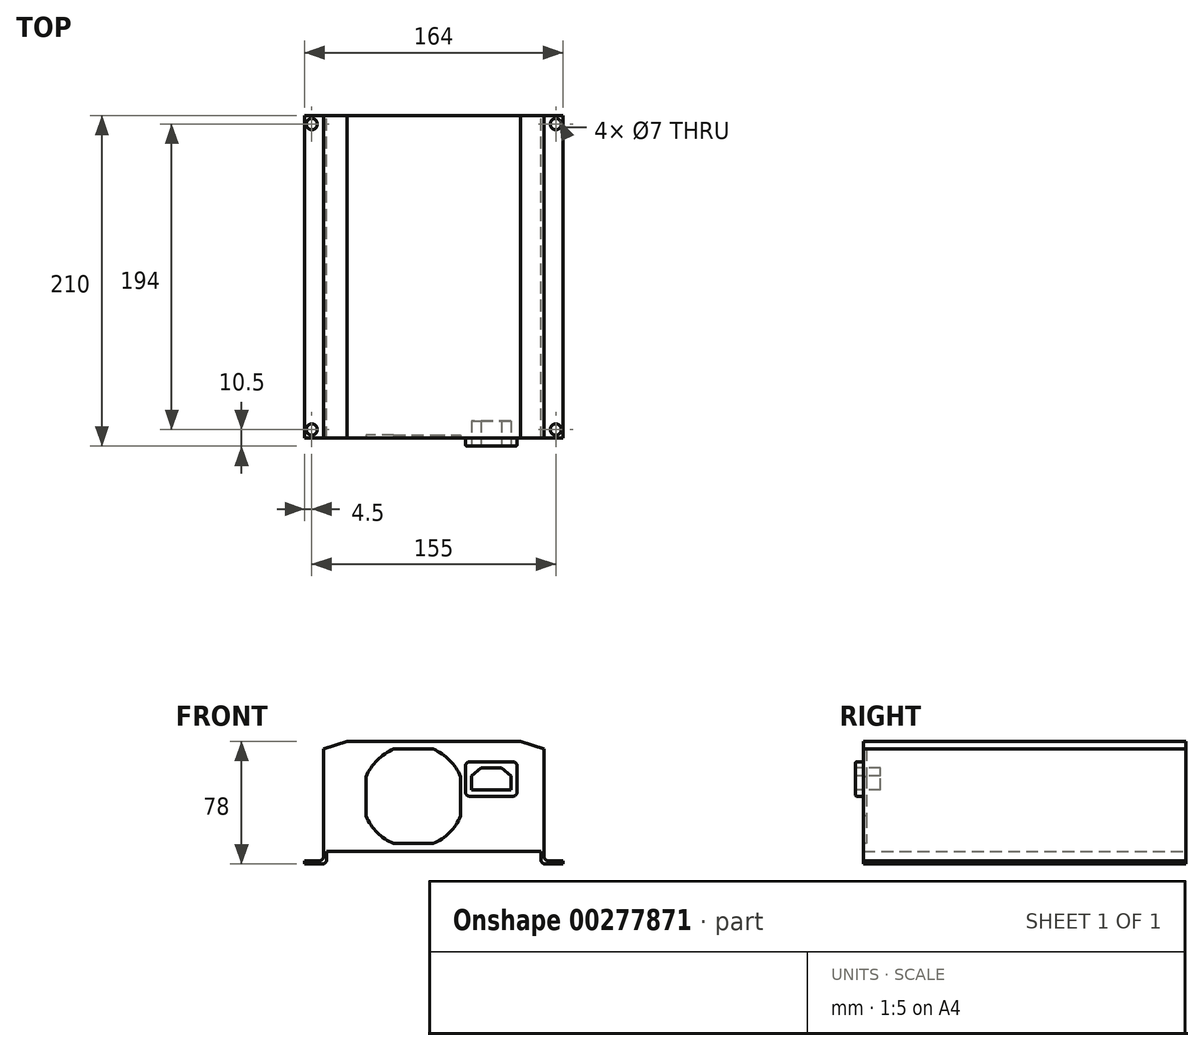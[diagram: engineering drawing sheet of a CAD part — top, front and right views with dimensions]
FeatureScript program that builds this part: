
annotation { "Feature Type Name" : "Feature", "Feature Type Description" : "" }
export const myFeature = defineFeature(function(context is Context, id is Id, definition is map)
    precondition{}
    {
        {
            var Q0;
            Q0=qCreatedBy(makeId("Front.planeOp"),FACE);
            var sketch = newSketch(context, id + "F0", { "sketchPlane" : qUnion([Q0])});
            skLineSegment(sketch, "E0", {"start": v(0, 70) * mm, "end": v(55, 70) * mm});
            skLineSegment(sketch, "E1", {"start": v(55, 70) * mm, "end": v(70, 65) * mm});
            skLineSegment(sketch, "E2", {"start": v(70, 65) * mm, "end": v(70, 0) * mm});
            skLineSegment(sketch, "E3", {"start": v(70, 0) * mm, "end": v(0, 0) * mm});
            skLineSegment(sketch, "E4.MirrorCS", {"start": v(0, 70) * mm, "end": v(-55, 70) * mm});
            skLineSegment(sketch, "E5.MirrorCS", {"start": v(-55, 70) * mm, "end": v(-70, 65) * mm});
            skLineSegment(sketch, "E6.MirrorCS", {"start": v(-70, 65) * mm, "end": v(-70, 0) * mm});
            skLineSegment(sketch, "E7.MirrorCS", {"start": v(-70, 0) * mm, "end": v(0, 0) * mm});
            skLineSegment(sketch, "E8", {"start": v(-70, 0) * mm, "end": v(-70, -3) * mm});
            skLineSegment(sketch, "E9", {"start": v(-73, -6) * mm, "end": v(-82, -6) * mm});
            skLineSegment(sketch, "E10", {"start": v(-82, -6) * mm, "end": v(-82, -8) * mm});
            skLineSegment(sketch, "E11", {"start": v(-82, -8) * mm, "end": v(-71, -8) * mm});
            skLineSegment(sketch, "E12", {"start": v(-68, -5) * mm, "end": v(-68, 0) * mm});
            skPoint(sketch, "E13.visualSharp", {"position": v(-70, -6) * mm});
            skArc(sketch, "E13.filletArc", {"start": v(-73, -6) * mm, "mid": v(-70.88, -5.12) * mm, "end": v(-70, -3) * mm});
            skPoint(sketch, "E14.visualSharp", {"position": v(-68, -8) * mm});
            skArc(sketch, "E14.filletArc", {"start": v(-71, -8) * mm, "mid": v(-68.88, -7.12) * mm, "end": v(-68, -5) * mm});
            skLineSegment(sketch, "E15.MirrorCS", {"start": v(82, -8) * mm, "end": v(71, -8) * mm});
            skLineSegment(sketch, "E16.MirrorCS", {"start": v(82, -6) * mm, "end": v(82, -8) * mm});
            skLineSegment(sketch, "E17.MirrorCS", {"start": v(73, -6) * mm, "end": v(82, -6) * mm});
            skArc(sketch, "E18.MirrorCS", {"start": v(73, -6) * mm, "mid": v(70.88, -5.12) * mm, "end": v(70, -3) * mm});
            skArc(sketch, "E19.MirrorCS", {"start": v(71, -8) * mm, "mid": v(68.88, -7.12) * mm, "end": v(68, -5) * mm});
            skLineSegment(sketch, "E20.MirrorCS", {"start": v(68, -5) * mm, "end": v(68, 0) * mm});
            skLineSegment(sketch, "E21.MirrorCS", {"start": v(70, 0) * mm, "end": v(70, -3) * mm});
            skSolve(sketch);
        }
        {
            var Q0;
            Q0 = qSketchRegion(id + "F0", true);
            extrude(context, id + "F1", {"entities" : qUnion([Q0]), "endBound" : BoundingType.SYMMETRIC, "depth" : 205 * mm});
        }
        {
            var Q0;
            Q0=makeQuery(id+"F1.opExtrude","SWEPT_FACE",FACE,{"disambiguationData":[OSD([sQuery(id+"F0.wireOp",EDGE,"E17.MirrorCS")])]});
            var sketch = newSketch(context, id + "F2", { "sketchPlane" : qUnion([Q0])});
            skCircle(sketch, "E22", {"center": v(77.5, -97) * mm, "radius": 3.5 * mm});
            skCircle(sketch, "E23.MirrorC", {"center": v(77.5, 97) * mm, "radius": 3.5 * mm});
            skCircle(sketch, "E24.MirrorC", {"center": v(-77.5, -97) * mm, "radius": 3.5 * mm});
            skCircle(sketch, "E25.MirrorC", {"center": v(-77.5, 97) * mm, "radius": 3.5 * mm});
            skSolve(sketch);
        }
        {
            var Q0;
            Q0 = qSketchRegion(id + "F2", true);
            extrude(context, id + "F3", {"entities" : qUnion([Q0]), "operationType" : NewBodyOperationType.REMOVE, "endBound" : BoundingType.UP_TO_NEXT, "oppositeDirection" : true, "depth" : 25 * mm});
        }
        {
            var Q0;
            Q0=makeQuery(id+"F1.opExtrude","CAP_FACE",FACE,{"disambiguationData":[OSD([sQuery(id+"F0.wireOp",EDGE,"E0"),sQuery(id+"F0.wireOp",EDGE,"E1"),sQuery(id+"F0.wireOp",EDGE,"E2"),sQuery(id+"F0.wireOp",EDGE,"E3"),sQuery(id+"F0.wireOp",EDGE,"E4.MirrorCS"),sQuery(id+"F0.wireOp",EDGE,"E5.MirrorCS"),sQuery(id+"F0.wireOp",EDGE,"E6.MirrorCS"),sQuery(id+"F0.wireOp",EDGE,"E7.MirrorCS"),sQuery(id+"F0.wireOp",EDGE,"E8"),sQuery(id+"F0.wireOp",EDGE,"E9"),sQuery(id+"F0.wireOp",EDGE,"E10"),sQuery(id+"F0.wireOp",EDGE,"E11"),sQuery(id+"F0.wireOp",EDGE,"E12"),sQuery(id+"F0.wireOp",EDGE,"E13.filletArc"),sQuery(id+"F0.wireOp",EDGE,"E14.filletArc"),sQuery(id+"F0.wireOp",EDGE,"E15.MirrorCS"),sQuery(id+"F0.wireOp",EDGE,"E16.MirrorCS"),sQuery(id+"F0.wireOp",EDGE,"E17.MirrorCS"),sQuery(id+"F0.wireOp",EDGE,"E18.MirrorCS"),sQuery(id+"F0.wireOp",EDGE,"E19.MirrorCS"),sQuery(id+"F0.wireOp",EDGE,"E20.MirrorCS"),sQuery(id+"F0.wireOp",EDGE,"E21.MirrorCS")])],"isStart":false});
            var sketch = newSketch(context, id + "F4", { "sketchPlane" : qUnion([Q0])});
            skLineSegment(sketch, "E26.bottom", {"start": v(23, 57) * mm, "end": v(50, 57) * mm});
            skLineSegment(sketch, "E26.top", {"start": v(23, 35) * mm, "end": v(50, 35) * mm});
            skLineSegment(sketch, "E26.left", {"start": v(20, 54) * mm, "end": v(20, 38) * mm});
            skLineSegment(sketch, "E26.right", {"start": v(53, 54) * mm, "end": v(53, 38) * mm});
            skPoint(sketch, "E27.visualSharp", {"position": v(53, 57) * mm});
            skArc(sketch, "E27.filletArc", {"start": v(53, 54) * mm, "mid": v(52.12, 56.12) * mm, "end": v(50, 57) * mm});
            skPoint(sketch, "E28.visualSharp", {"position": v(53, 35) * mm});
            skArc(sketch, "E28.filletArc", {"start": v(50, 35) * mm, "mid": v(52.12, 35.88) * mm, "end": v(53, 38) * mm});
            skPoint(sketch, "E29.visualSharp", {"position": v(20, 35) * mm});
            skArc(sketch, "E29.filletArc", {"start": v(20, 38) * mm, "mid": v(20.88, 35.88) * mm, "end": v(23, 35) * mm});
            skPoint(sketch, "E30.visualSharp", {"position": v(20, 57) * mm});
            skArc(sketch, "E30.filletArc", {"start": v(23, 57) * mm, "mid": v(20.88, 56.12) * mm, "end": v(20, 54) * mm});
            skSolve(sketch);
        }
        {
            var Q0;
            Q0 = qSketchRegion(id + "F4", true);
            extrude(context, id + "F5", {"entities" : qUnion([Q0]), "operationType" : NewBodyOperationType.ADD, "depth" : 5 * mm});
        }
        {
            var Q0;
            Q0=makeQuery(id+"F5.opExtrude","CAP_FACE",FACE,{"disambiguationData":[OSD([sQuery(id+"F4.wireOp",EDGE,"E26.bottom"),sQuery(id+"F4.wireOp",EDGE,"E26.top"),sQuery(id+"F4.wireOp",EDGE,"E26.left"),sQuery(id+"F4.wireOp",EDGE,"E26.right"),sQuery(id+"F4.wireOp",EDGE,"E27.filletArc"),sQuery(id+"F4.wireOp",EDGE,"E28.filletArc"),sQuery(id+"F4.wireOp",EDGE,"E29.filletArc"),sQuery(id+"F4.wireOp",EDGE,"E30.filletArc")])],"isStart":false});
            fillet(context, id + "F6", {"entities" : qUnion([Q0]), "radius" : 1 * mm, "tangentPropagation" : true, "allowEdgeOverflow" : false});
        }
        {
            var Q0;
            Q0=makeQuery(id+"F5.opExtrude","CAP_FACE",FACE,{"disambiguationData":[OSD([sQuery(id+"F4.wireOp",EDGE,"E26.bottom"),sQuery(id+"F4.wireOp",EDGE,"E26.top"),sQuery(id+"F4.wireOp",EDGE,"E26.left"),sQuery(id+"F4.wireOp",EDGE,"E26.right"),sQuery(id+"F4.wireOp",EDGE,"E27.filletArc"),sQuery(id+"F4.wireOp",EDGE,"E28.filletArc"),sQuery(id+"F4.wireOp",EDGE,"E29.filletArc"),sQuery(id+"F4.wireOp",EDGE,"E30.filletArc")])],"isStart":false});
            var sketch = newSketch(context, id + "F7", { "sketchPlane" : qUnion([Q0])});
            skLineSegment(sketch, "E31", {"start": v(30, 53) * mm, "end": v(43, 53) * mm});
            skLineSegment(sketch, "E32", {"start": v(43, 53) * mm, "end": v(49, 48) * mm});
            skLineSegment(sketch, "E33", {"start": v(49, 48) * mm, "end": v(49, 39) * mm});
            skLineSegment(sketch, "E34", {"start": v(49, 39) * mm, "end": v(24, 39) * mm});
            skLineSegment(sketch, "E35", {"start": v(24, 39) * mm, "end": v(24, 48) * mm});
            skLineSegment(sketch, "E36", {"start": v(24, 48) * mm, "end": v(30, 53) * mm});
            skSolve(sketch);
        }
        {
            var Q0;
            Q0 = qSketchRegion(id + "F7", true);
            extrude(context, id + "F8", {"entities" : qUnion([Q0]), "operationType" : NewBodyOperationType.REMOVE, "oppositeDirection" : true, "depth" : 16 * mm});
        }
        {
            var Q0;
            Q0=makeQuery(id+"F1.opExtrude","CAP_FACE",FACE,{"disambiguationData":[OSD([sQuery(id+"F0.wireOp",EDGE,"E0"),sQuery(id+"F0.wireOp",EDGE,"E1"),sQuery(id+"F0.wireOp",EDGE,"E2"),sQuery(id+"F0.wireOp",EDGE,"E3"),sQuery(id+"F0.wireOp",EDGE,"E4.MirrorCS"),sQuery(id+"F0.wireOp",EDGE,"E5.MirrorCS"),sQuery(id+"F0.wireOp",EDGE,"E6.MirrorCS"),sQuery(id+"F0.wireOp",EDGE,"E7.MirrorCS"),sQuery(id+"F0.wireOp",EDGE,"E8"),sQuery(id+"F0.wireOp",EDGE,"E9"),sQuery(id+"F0.wireOp",EDGE,"E10"),sQuery(id+"F0.wireOp",EDGE,"E11"),sQuery(id+"F0.wireOp",EDGE,"E12"),sQuery(id+"F0.wireOp",EDGE,"E13.filletArc"),sQuery(id+"F0.wireOp",EDGE,"E14.filletArc"),sQuery(id+"F0.wireOp",EDGE,"E15.MirrorCS"),sQuery(id+"F0.wireOp",EDGE,"E16.MirrorCS"),sQuery(id+"F0.wireOp",EDGE,"E17.MirrorCS"),sQuery(id+"F0.wireOp",EDGE,"E18.MirrorCS"),sQuery(id+"F0.wireOp",EDGE,"E19.MirrorCS"),sQuery(id+"F0.wireOp",EDGE,"E20.MirrorCS"),sQuery(id+"F0.wireOp",EDGE,"E21.MirrorCS")])],"isStart":false});
            var sketch = newSketch(context, id + "F9", { "sketchPlane" : qUnion([Q0])});
            skArc(sketch, "E37", {"start": v(17, 47.5) * mm, "mid": v(9.98, 57.98) * mm, "end": v(-0.5, 65) * mm});
            skLineSegment(sketch, "E38", {"start": v(-25.5, 65) * mm, "end": v(-0.5, 65) * mm});
            skLineSegment(sketch, "E39", {"start": v(-0.5, 5) * mm, "end": v(-25.5, 5) * mm});
            skLineSegment(sketch, "E40", {"start": v(17, 47.5) * mm, "end": v(17, 22.5) * mm});
            skLineSegment(sketch, "E41", {"start": v(-43, 47.5) * mm, "end": v(-43, 22.5) * mm});
            skArc(sketch, "E42.trimOffspring", {"start": v(-25.5, 65) * mm, "mid": v(-35.98, 57.98) * mm, "end": v(-43, 47.5) * mm});
            skArc(sketch, "E43.trimOffspring", {"start": v(-43, 22.5) * mm, "mid": v(-35.98, 12.02) * mm, "end": v(-25.5, 5) * mm});
            skArc(sketch, "E44.trimOffspring", {"start": v(-0.5, 5) * mm, "mid": v(9.98, 12.02) * mm, "end": v(17, 22.5) * mm});
            skSolve(sketch);
        }
        {
            var Q0;
            Q0 = qSketchRegion(id + "F9", true);
            extrude(context, id + "F10", {"entities" : qUnion([Q0]), "operationType" : NewBodyOperationType.REMOVE, "oppositeDirection" : true, "depth" : 2 * mm});
        }
    });
